AUTODESK INVENTOR PART (.ipt)
format: ipt  version: 2011 SP2 (Build 150309200, 309)  size: 145,920 bytes
history: native  units: mm
features: sketch x3, extrude x2, hole x1, fillet x1
ambient origin geometry x8: Origin, YZ Plane, XZ Plane, XY Plane, X Axis, Y Axis, Z Axis, Center Point
bodies: Solid1 (feature_tree)
feature tree (7):
  extrude  "Extrusion1"  Depth=33.421041mm
  extrude  "Extrusion2"  Depth=5.21368mm
  hole  "Hole1"  [1 undecoded]
  fillet  "Fillet1"  Radius=26.80368mm
  sketch  "Sketch1"  dims[d0=25.4mm d1=33.421041mm]
  sketch  "Sketch2"  dims[d2=10.02632mm d3=5.21368mm]
  sketch  "Sketch3"  dims[d4=27.739467mm d5=26.268959mm d7=26.80368mm d8=37.297893mm d9=26.335787mm d10=24.531041mm d11=43.915254mm d12=32.752538mm d13=41.375254mm d6=37.297893mm d14=27.739467mm d15=26.80368mm d16=20.0mm d17=0.0mm d18=4.0mm d19=10.0mm d20=0.0mm d21=3.4mm d22=6.0mm d23=4.4mm d24=3.0mm d25=90.0deg d26=8.0mm d27=20.594885mm d28=2.0mm]
note: 1 required parameter value undecoded (feature->parameter linkage not recoverable at this tier; creation-order binding heuristic only, values carry confidence <= 0.55)
